# Revit family: LUXI_WATERPROOF LIGHT_VT
name_source: partatom
category: Apparecchi per illuminazione
revit_build: Autodesk Revit 2016 (Build: 20161004_0715(x64)
units: mm (PartAtom-declared; Revit-internal decimal feet)

## family parameters
Condiviso = No
Host = Superficie
Numero OmniClass = 23.80.70.00
Punto di calcolo locali = Sì
Quota connettore circolare = Usa diametro
Sorgente d'illuminazione = Sì
Taglio con vuoti quando caricato = No
Tipo di parte = Normale
Titolo OmniClass = Lighting

## types (4) — shared parameters
Alimentatore = Incluso
Alimentazione = 220-240V AC / 50-60 Hz
Angolo inclinazione = -90.00°
Carico apparente = 70 VA
Certificazioni = CE / RohS
Classe di efficienza energetica = A+
Classe di protezione = I
Classe di rischio fotobiologico = Esente (RG0)
Colore = Grigio
Descrizione = Plafoniera stagna
Dimensioni = 1490x112x89
Emetti da larghezza rettangolo = 83 mm
Emetti da lunghezza rettangolo = 1430 mm  [stored 4.6916 ft]
Fattore di correzione di potenza = ≥0,95 (typ.)
Filtro dei colori = 16777215
Garanzia = 5 anni
Grado di protezione = IP 66
H = 89 mm  [stored 0.291995 ft]
IFCExportAs = IfcLightFixtureType
Indice di resa cromatica = ≥80 (typ.)
Larghezza = 112 mm  [stored 0.367454 ft]
Lunghezza = 1490 mm  [stored 4.88845 ft]
Masterformat 2016 Codice = 26.50.00
Masterformat 2016 Descrizione = Lighting
Materiale 1 = Alluminio Pressofuso_Grigio
Materiale 2 = Alluminio Pressofuso_Grigio
Modello = Serie WT | Waterproof Light
OFF1 = 30 mm  [stored 0.0984252 ft]
Peso = 4.80 kg
Potenza = 70 W
Produttore = Luxi Illuminazione S.r.l.
Prospetto di default = 2000 mm  [stored 6.56168 ft]
Protezione agli urti = IK07 (2 Joule)
Rendi la forma visibile nel rendering = No
Revisione = 3
Sistema di illuminazione = luce diretta
Sorgente = LED SMD
Step MacAdam (SDCM) = <4
Temperatura di esercizio = -25°C / +40°C
Tipologie di installazione = Parete / Soffitto
URL = https://www.luxi.lighting
Uniclass 2015 Codice = EF_70_80
Uniclass 2015 Descrizione = Lighting
Variazione temperatura colore lampada con luminosità attenuata = <Nessuno>
Vita utile = L70B20 50.000ore

## per-type parameters (varying)
| type | File diagramma fotometrico | Materiale 3 | Ottiche | Regolazione del flusso luminoso |
| WPVT070090G840 | WPVT070090G840 Luxi Serie VT 70W BA90X90 1500MM GR 840.IES | PC Prismatizzato | 90° | Non disponibile |
| WPVT070411G840 | WPVT070411G840 Luxi Serie VT 70W BA40X110 1500MM GR 840.IES | Vetro Prismatizzato | 40X110° | Non disponibile |
| WPVT070090G840DA | WPVT070090G840 Luxi Serie VT 70W BA90X90 1500MM GR 840.IES | PC Prismatizzato | 90° | DALI |
| WPVT070411G840DA | WPVT070411G840 Luxi Serie VT 70W BA40X110 1500MM GR 840.IES | Vetro Prismatizzato | 40X110° | DALI |

note: column(s) folded — value = type name in every type: Articolo

note: [stored X ft] marks values corroborated as IEEE doubles in the binary element streams (Revit-internal decimal feet)
